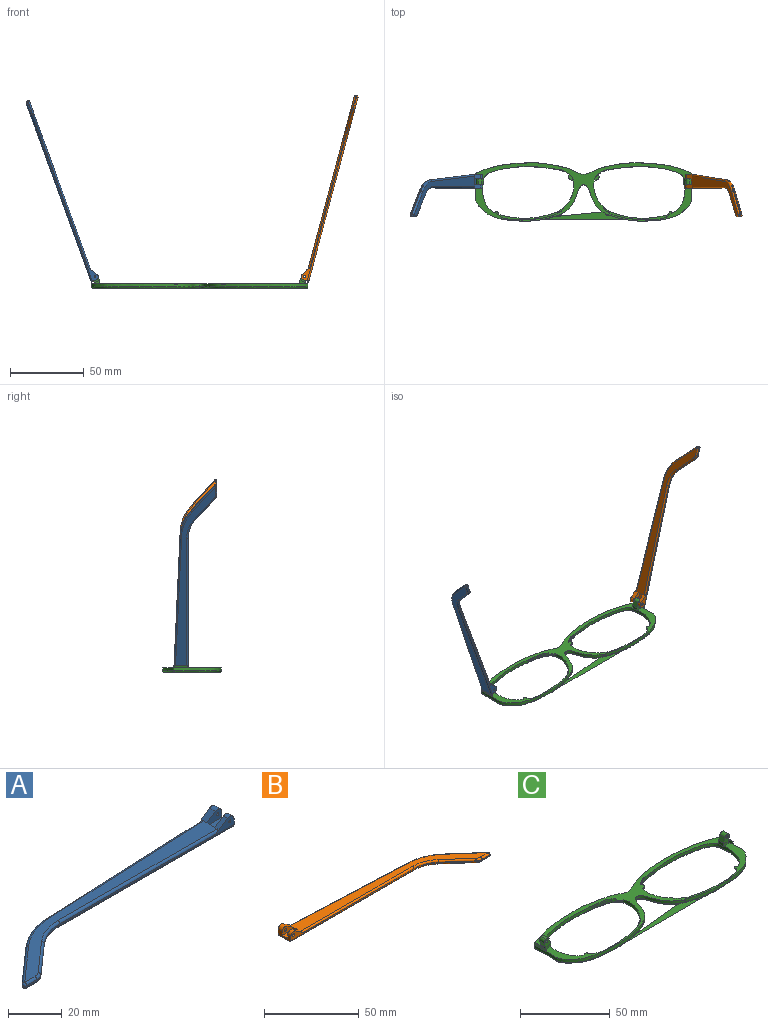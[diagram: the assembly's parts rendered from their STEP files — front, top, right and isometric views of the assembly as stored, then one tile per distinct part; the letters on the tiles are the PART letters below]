
ASSEMBLY  parts=3 mates=2
PART A: 43 faces, bbox 130.2x29.5x5.9 mm
  f0: plane 9.62x3.72mm, normal (1,0,0), area 24.7mm2, adj f1,f3,f4,f5,f10,f16,f18,f28
  f1: cylinder r=2.2mm len=3.45mm, axis (0,-1,0), area 11mm2, adj f0,f2,f4,f37
  f2: plane 6.01x3.91mm, normal (-0.55,0,0.84), area 12.7mm2, adj f1,f4,f9,f19,f37
  f3: plane 2.26x0.1mm, normal (0,0,1), area 0.1mm2, adj f0,f5,f18
  f4: plane 92.1x4.9mm, normal (0,-1,0), area 79.9mm2, adj f0,f1,f2,f14,f19,f36,f42
  f5: plane 93.42x4.13mm, normal (-0.04,1,0), area 64.8mm2, adj f0,f3,f11,f15,f17,f27,f28
  f6: plane 17.82x15.72mm, normal (-0.66,0.75,0), area 14.3mm2, adj f11,f12,f25,f30
  f7: plane 5.46x0.6mm, normal (0,-1,0), area 3.3mm2, adj f12,f13,f23,f32
  f8: plane 14.99x13.23mm, normal (0.66,-0.75,0), area 12mm2, adj f13,f14,f21,f34
  f9: plane 121.18x26.73mm, normal (0,0,1), area 627.7mm2, adj f2,f17,f19,f20,f21,f22,f23,f25
  f10: plane 129.1x27.08mm, normal (0,0,-1), area 686.5mm2, adj f0,f28,f29,f30,f32,f33,f34,f35
  f11: cylinder r=30mm len=18.52mm, axis (0,0,-1), area 12.2mm2, adj f5,f6,f26,f29
  f12: cylinder r=1mm len=1.75mm, axis (0,0,-1), area 1.5mm2, adj f6,f7,f24,f31
  f13: cylinder r=5mm len=3.31mm, axis (0,0,-1), area 2.2mm2, adj f7,f8,f22,f33
  f14: cylinder r=20mm len=13.23mm, axis (0,0,1), area 8.7mm2, adj f4,f8,f20,f35
  f15: plane 5.66x0.25mm, normal (0,0,-1), area 0.7mm2, adj f5,f17,f18
  f16: cylinder r=2.2mm len=3.45mm, axis (0,-1,0), area 14.8mm2, adj f0,f17,f18,f38
  f17: plane 6.01x3.91mm, normal (-0.55,0,0.84), area 16.9mm2, adj f5,f9,f15,f16,f18,f27,f38
  f18: plane 7.92x3.3mm, normal (0,1,0), area 15.9mm2, adj f0,f3,f15,f16,f17,f41
  f19: cylinder r=1mm len=84.18mm, axis (-1,0,0), area 131.4mm2, adj f2,f4,f9,f20
  f20: torus R=21mm, axis (0,0,1), area 23.1mm2, adj f9,f14,f19,f21
  f21: cylinder r=1mm len=15.65mm, axis (-0.75,-0.66,0), area 31.4mm2, adj f8,f9,f20,f22
  f22: torus R=4mm, axis (0,0,1), area 5.3mm2, adj f9,f13,f21,f23
  f23: cylinder r=1mm len=5.46mm, axis (-1,0,0), area 8.6mm2, adj f7,f9,f22,f24
  f24: sphere r=1mm, area 2.4mm2, adj f12,f23,f25
  f25: cylinder r=1mm len=18.48mm, axis (0.75,0.66,0), area 37.3mm2, adj f6,f9,f24,f26
  f26: torus R=29mm, axis (0,0,1), area 31.6mm2, adj f9,f11,f25,f27
  f27: cylinder r=1mm len=85.5mm, axis (1,0.04,0), area 133.5mm2, adj f5,f9,f17,f26
  f28: cylinder r=1mm len=93.46mm, axis (-1,-0.04,0), area 146.9mm2, adj f0,f5,f10,f29
  f29: torus R=29mm, axis (0,0,1), area 31.6mm2, adj f10,f11,f28,f30
  f30: cylinder r=1mm len=18.48mm, axis (-0.75,-0.66,0), area 37.3mm2, adj f6,f10,f29,f31
  f31: sphere r=1mm, area 2.4mm2, adj f12,f30,f32
  f32: cylinder r=1mm len=5.46mm, axis (1,0,0), area 8.6mm2, adj f7,f10,f31,f33
  f33: torus R=4mm, axis (0,0,1), area 5.3mm2, adj f10,f13,f32,f34
  f34: cylinder r=1mm len=15.65mm, axis (0.75,0.66,0), area 31.4mm2, adj f8,f10,f33,f35
  f35: torus R=21mm, axis (0,0,1), area 23.1mm2, adj f10,f14,f34,f36
  f36: cylinder r=1mm len=92.1mm, axis (1,0,0), area 144.7mm2, adj f0,f4,f10,f35
  f37: plane 7.92x4.7mm, normal (0,1,0), area 27mm2, adj f0,f1,f2,f39,f40,f42
  f38: plane 7.92x4.7mm, normal (0,-1,0), area 27mm2, adj f0,f16,f17,f39,f40,f41
  f39: plane 7.92x4.1mm, normal (0,0,1), area 32.5mm2, adj f0,f37,f38,f40
  f40: plane 4.1x1.4mm, normal (1,0,0), area 5.7mm2, adj f9,f37,f38,f39
  f41: cylinder r=0.5mm len=3.1mm, axis (0,-1,0), area 9.7mm2, adj f18,f38
  f42: cylinder r=0.5mm len=2.3mm, axis (0,-1,0), area 7.2mm2, adj f4,f37
PART B: 43 faces, bbox 130.2x29.5x5.9 mm
  f0: plane 9.62x3.72mm, normal (-1,0,0), area 24.7mm2, adj f1,f3,f4,f5,f10,f16,f18,f28
  f1: cylinder r=2.2mm len=3.45mm, axis (0,-1,0), area 11mm2, adj f0,f2,f4,f37
  f2: plane 6.01x3.91mm, normal (0.55,0,0.84), area 12.7mm2, adj f1,f4,f9,f19,f37
  f3: plane 2.26x0.1mm, normal (0,0,1), area 0.1mm2, adj f0,f5,f18
  f4: plane 92.1x4.9mm, normal (0,-1,0), area 78.2mm2, adj f0,f1,f2,f14,f19,f36,f42
  f5: plane 93.42x4.13mm, normal (0.04,1,0), area 64.8mm2, adj f0,f3,f11,f15,f17,f27,f28
  f6: plane 17.82x15.72mm, normal (0.66,0.75,0), area 14.3mm2, adj f11,f12,f25,f30
  f7: plane 5.46x0.6mm, normal (0,-1,0), area 3.3mm2, adj f12,f13,f23,f32
  f8: plane 14.99x13.23mm, normal (-0.66,-0.75,0), area 12mm2, adj f13,f14,f21,f34
  f9: plane 121.18x26.73mm, normal (0,0,1), area 627.7mm2, adj f2,f17,f19,f20,f21,f22,f23,f25
  f10: plane 129.1x27.08mm, normal (0,0,-1), area 686.5mm2, adj f0,f28,f29,f30,f32,f33,f34,f35
  f11: cylinder r=30mm len=18.52mm, axis (0,0,-1), area 12.2mm2, adj f5,f6,f26,f29
  f12: cylinder r=1mm len=1.75mm, axis (0,0,-1), area 1.5mm2, adj f6,f7,f24,f31
  f13: cylinder r=5mm len=3.31mm, axis (0,0,-1), area 2.2mm2, adj f7,f8,f22,f33
  f14: cylinder r=20mm len=13.23mm, axis (0,0,1), area 8.7mm2, adj f4,f8,f20,f35
  f15: plane 5.66x0.25mm, normal (0,0,-1), area 0.7mm2, adj f5,f17,f18
  f16: cylinder r=2.2mm len=3.45mm, axis (0,-1,0), area 14.8mm2, adj f0,f17,f18,f38
  f17: plane 6.01x3.91mm, normal (0.55,0,0.84), area 16.9mm2, adj f5,f9,f15,f16,f18,f27,f38
  f18: plane 7.92x3.3mm, normal (0,1,0), area 14.3mm2, adj f0,f3,f15,f16,f17,f41
  f19: cylinder r=1mm len=84.18mm, axis (1,0,0), area 131.4mm2, adj f2,f4,f9,f20
  f20: torus R=21mm, axis (0,0,1), area 23.1mm2, adj f9,f14,f19,f21
  f21: cylinder r=1mm len=15.65mm, axis (0.75,-0.66,0), area 31.4mm2, adj f8,f9,f20,f22
  f22: torus R=4mm, axis (0,0,1), area 5.3mm2, adj f9,f13,f21,f23
  f23: cylinder r=1mm len=5.46mm, axis (1,0,0), area 8.6mm2, adj f7,f9,f22,f24
  f24: sphere r=1mm, area 2.4mm2, adj f12,f23,f25
  f25: cylinder r=1mm len=18.48mm, axis (-0.75,0.66,0), area 37.3mm2, adj f6,f9,f24,f26
  f26: torus R=29mm, axis (0,0,1), area 31.6mm2, adj f9,f11,f25,f27
  f27: cylinder r=1mm len=85.5mm, axis (-1,0.04,0), area 133.5mm2, adj f5,f9,f17,f26
  f28: cylinder r=1mm len=93.46mm, axis (1,-0.04,0), area 146.9mm2, adj f0,f5,f10,f29
  f29: torus R=29mm, axis (0,0,1), area 31.6mm2, adj f10,f11,f28,f30
  f30: cylinder r=1mm len=18.48mm, axis (0.75,-0.66,0), area 37.3mm2, adj f6,f10,f29,f31
  f31: sphere r=1mm, area 2.4mm2, adj f12,f30,f32
  f32: cylinder r=1mm len=5.46mm, axis (-1,0,0), area 8.6mm2, adj f7,f10,f31,f33
  f33: torus R=4mm, axis (0,0,1), area 5.3mm2, adj f10,f13,f32,f34
  f34: cylinder r=1mm len=15.65mm, axis (-0.75,0.66,0), area 31.4mm2, adj f8,f10,f33,f35
  f35: torus R=21mm, axis (0,0,1), area 23.1mm2, adj f10,f14,f34,f36
  f36: cylinder r=1mm len=92.1mm, axis (-1,0,0), area 144.7mm2, adj f0,f4,f10,f35
  f37: plane 7.92x4.7mm, normal (0,1,0), area 25.4mm2, adj f0,f1,f2,f39,f40,f42
  f38: plane 7.92x4.7mm, normal (0,-1,0), area 25.4mm2, adj f0,f16,f17,f39,f40,f41
  f39: plane 7.92x4.1mm, normal (0,0,1), area 32.5mm2, adj f0,f37,f38,f40
  f40: plane 4.1x1.4mm, normal (-1,0,0), area 5.7mm2, adj f9,f37,f38,f39
  f41: cylinder r=0.88mm len=3.1mm, axis (0,-1,0), area 17mm2, adj f18,f38
  f42: cylinder r=0.88mm len=2.3mm, axis (0,-1,0), area 12.6mm2, adj f4,f37
PART C: 86 faces, bbox 148.1x40x10.2 mm
  f0: plane 1.81x0.58mm, normal (-0.02,-1,0), area 0.5mm2, adj f3,f34,f43
  f1: plane 1.81x0.58mm, normal (0,1,0), area 0.5mm2, adj f25,f33,f43
  f2: extruded ~43.79x32.28mm, area 146.9mm2, adj f7,f10,f11,f12,f13,f14,f19,f41
  f3: extruded ~73.47x39.61mm, area 288mm2, adj f0,f4,f13,f16,f17,f18,f26,f39
  f4: extruded ~34.8x7.92mm, area 72mm2, adj f3,f13,f15,f48
  f5: extruded ~23.36x6.33mm, area 51.8mm2, adj f7,f10,f11,f12,f13,f14,f35,f36
  f6: plane 145.02x37.66mm, normal (0,0,-1), area 433.4mm2, adj f14,f15,f16,f17,f56,f57,f58,f59
  f7: extruded ~45.22x8.67mm, area 48.7mm2, adj f2,f5,f8,f12
  f8: plane 45.37x8.78mm, normal (0,0,1), area 54.3mm2, adj f7,f14
  f9: plane 13.74x3.47mm, normal (0,0,1), area 2.6mm2, adj f10,f14
  f10: extruded ~13.38x3.11mm, area 13.9mm2, adj f2,f5,f9,f11
  f11: extruded ~13.38x3.11mm, area 13.9mm2, adj f2,f5,f10,f13
  f12: extruded ~45.22x8.67mm, area 47.4mm2, adj f2,f5,f7,f13,f37,f38,f41,f42
  f13: plane 147.17x39.75mm, normal (0,0,1), area 1008.8mm2, adj f2,f3,f4,f5,f11,f12,f20,f21
  f14: bspline ~63.93x37.14mm, area 257.8mm2, adj f2,f5,f6,f8,f9,f16
  f15: bspline ~60.33x9.85mm, area 56.6mm2, adj f4,f6,f17,f57
  f16: bspline ~73.71x31.86mm, area 168.9mm2, adj f3,f6,f14,f18,f58
  f17: bspline ~58.8x8.12mm, area 61.8mm2, adj f3,f6,f15,f18
  f18: bspline ~1x0.99mm, area 0.3mm2, adj f3,f16,f17
  f19: plane 3.99x0.65mm, normal (0,0,-1), area 1.5mm2, adj f2,f21,f22
  f20: plane 6.93x5.07mm, normal (0,1,0), area 23.5mm2, adj f13,f21,f23,f24,f27,f29,f30,f31
  f21: plane 4x2.36mm, normal (-1,0,0), area 9.5mm2, adj f13,f19,f20,f22,f24
  f22: plane 3.75x2.36mm, normal (0,-1,0), area 6.3mm2, adj f13,f19,f21,f23,f24,f28
  f23: plane 4x1mm, normal (1,0,0), area 4mm2, adj f13,f20,f22,f29
  f24: plane 4x0.12mm, normal (0.34,0,0.94), area 0.5mm2, adj f20,f21,f22,f27
  f25: plane 8.84x1.6mm, normal (0.94,0,-0.34), area 15mm2, adj f1,f13,f34,f43
  f26: plane 9.76x1.81mm, normal (-1,0,0), area 17.7mm2, adj f3,f13,f33,f43
  f27: plane 4x3.31mm, normal (-0.94,0,0.34), area 14.1mm2, adj f20,f24,f28,f31
  f28: plane 5.93x4.95mm, normal (0,-1,0), area 17.2mm2, adj f22,f27,f29,f30,f31,f32
  f29: plane 4x3.31mm, normal (0.94,0,-0.34), area 14.1mm2, adj f20,f23,f28,f30
  f30: cylinder r=1.98mm len=4mm, axis (0,-1,0), area 12.2mm2, adj f20,f28,f29,f31
  f31: cylinder r=1.98mm len=4mm, axis (0,1,0), area 12.2mm2, adj f20,f27,f28,f30
  f32: cylinder r=0.88mm len=4mm, axis (0,-1,0), area 22mm2, adj f20,f28
  f33: cylinder r=1mm len=1.81mm, axis (0,0,1), area 0.3mm2, adj f1,f13,f26,f43
  f34: cone r=1mm half-angle=20deg, axis (0,0,1), area 0mm2, adj f0,f13,f25,f43
  f35: plane 3.96x3.19mm, normal (0,0,-1), area 7.5mm2, adj f5,f36
  f36: cylinder r=2.28mm len=3.93mm, axis (0,0,1), area 3.2mm2, adj f5,f13,f35
  f37: cylinder r=1.3mm len=1.78mm, axis (0,0,1), area 1.3mm2, adj f12,f13,f38
  f38: plane 1.79x1.31mm, normal (0,0,-1), area 0.9mm2, adj f12,f37
  f39: cylinder r=1.3mm len=2.21mm, axis (0,0,1), area 1.5mm2, adj f3,f13,f40
  f40: plane 2.21x1.33mm, normal (0,0,-1), area 1.4mm2, adj f3,f39
  f41: plane 2.48x1.93mm, normal (0,0,-1), area 2.6mm2, adj f2,f12,f42
  f42: cylinder r=1.3mm len=2.47mm, axis (0,0,1), area 2.1mm2, adj f2,f12,f13,f41
  f43: plane 9.77x0.6mm, normal (0.34,0,0.94), area 5.6mm2, adj f0,f1,f3,f25,f26,f33,f34
  f44: plane 1.81x0.58mm, normal (0.02,-1,0), area 0.5mm2, adj f47,f76,f85
  f45: plane 1.81x0.58mm, normal (0,1,0), area 0.5mm2, adj f67,f75,f85
  f46: extruded ~43.79x32.28mm, area 146.9mm2, adj f13,f50,f53,f54,f55,f56,f61,f83
  f47: extruded ~73.47x39.61mm, area 288mm2, adj f3,f13,f44,f48,f58,f59,f60,f68
  f48: extruded ~34.8x7.92mm, area 72mm2, adj f4,f13,f47,f57
  f49: extruded ~23.36x6.33mm, area 51.8mm2, adj f13,f50,f53,f54,f55,f56,f77,f78
  f50: extruded ~45.22x8.67mm, area 48.7mm2, adj f46,f49,f51,f55
  f51: plane 45.37x8.78mm, normal (0,0,1), area 54.3mm2, adj f50,f56
  f52: plane 13.74x3.47mm, normal (0,0,1), area 2.6mm2, adj f53,f56
  f53: extruded ~13.38x3.11mm, area 13.9mm2, adj f46,f49,f52,f54
  f54: extruded ~13.38x3.11mm, area 13.9mm2, adj f13,f46,f49,f53
  f55: extruded ~45.22x8.67mm, area 47.4mm2, adj f13,f46,f49,f50,f79,f80,f83,f84
  f56: bspline ~63.93x37.14mm, area 257.8mm2, adj f6,f46,f49,f51,f52,f58
  f57: bspline ~60.33x9.85mm, area 56.6mm2, adj f6,f15,f48,f59
  f58: bspline ~73.71x31.86mm, area 168.8mm2, adj f6,f16,f47,f56,f60
  f59: bspline ~58.8x8.12mm, area 61.8mm2, adj f6,f47,f57,f60
  f60: bspline ~1x0.99mm, area 0.3mm2, adj f47,f58,f59
  f61: plane 3.99x0.65mm, normal (0,0,-1), area 1.5mm2, adj f46,f63,f64
  f62: plane 6.93x5.07mm, normal (0,1,0), area 23.5mm2, adj f13,f63,f65,f66,f69,f71,f72,f73
  f63: plane 4x2.36mm, normal (1,0,0), area 9.5mm2, adj f13,f61,f62,f64,f66
  f64: plane 3.75x2.36mm, normal (0,-1,0), area 6.3mm2, adj f13,f61,f63,f65,f66,f70
  f65: plane 4x1mm, normal (-1,0,0), area 4mm2, adj f13,f62,f64,f71
  f66: plane 4x0.12mm, normal (-0.34,0,0.94), area 0.5mm2, adj f62,f63,f64,f69
  f67: plane 8.84x1.6mm, normal (-0.94,0,-0.34), area 15mm2, adj f13,f45,f76,f85
  f68: plane 9.76x1.81mm, normal (1,0,0), area 17.7mm2, adj f13,f47,f75,f85
  f69: plane 4x3.31mm, normal (0.94,0,0.34), area 14.1mm2, adj f62,f66,f70,f73
  f70: plane 5.93x4.95mm, normal (0,-1,0), area 17.2mm2, adj f64,f69,f71,f72,f73,f74
  f71: plane 4x3.31mm, normal (-0.94,0,-0.34), area 14.1mm2, adj f62,f65,f70,f72
  f72: cylinder r=1.98mm len=4mm, axis (0,-1,0), area 12.2mm2, adj f62,f70,f71,f73
  f73: cylinder r=1.98mm len=4mm, axis (0,1,0), area 12.2mm2, adj f62,f69,f70,f72
  f74: cylinder r=0.88mm len=4mm, axis (0,-1,0), area 22mm2, adj f62,f70
  f75: cylinder r=1mm len=1.81mm, axis (0,0,1), area 0.3mm2, adj f13,f45,f68,f85
  f76: cone r=1mm half-angle=20deg, axis (0,0,1), area 0mm2, adj f13,f44,f67,f85
  f77: plane 3.96x3.19mm, normal (0,0,-1), area 7.5mm2, adj f49,f78
  f78: cylinder r=2.28mm len=3.93mm, axis (0,0,1), area 3.2mm2, adj f13,f49,f77
  f79: cylinder r=1.3mm len=1.78mm, axis (0,0,1), area 1.3mm2, adj f13,f55,f80
  f80: plane 1.79x1.31mm, normal (0,0,-1), area 0.9mm2, adj f55,f79
  f81: cylinder r=1.3mm len=2.21mm, axis (0,0,1), area 1.5mm2, adj f13,f47,f82
  f82: plane 2.21x1.33mm, normal (0,0,-1), area 1.4mm2, adj f47,f81
  f83: plane 2.48x1.93mm, normal (0,0,-1), area 2.6mm2, adj f46,f55,f84
  f84: cylinder r=1.3mm len=2.47mm, axis (0,0,1), area 2.1mm2, adj f13,f46,f55,f83
  f85: plane 9.77x0.6mm, normal (-0.34,0,0.94), area 5.6mm2, adj f44,f45,f47,f67,f68,f75,f76
PLACE A rot(axis=(0,1,0),70deg) t=(-84.87,-5.75,55.97)mm
PLACE B rot(axis=(0,-1,0),75deg) t=(68.2,-5.75,-61.61)mm
PLACE C t=(10.15,-1.13,-5.77)mm
MATE revolute A.f1 <-> C.f73  axis (0,-1,0) through (-60.99,2.72,1.18)mm
MATE revolute B.f41 <-> C.f30  axis (0,-1,0) through (81.2,2.72,1.21)mm
